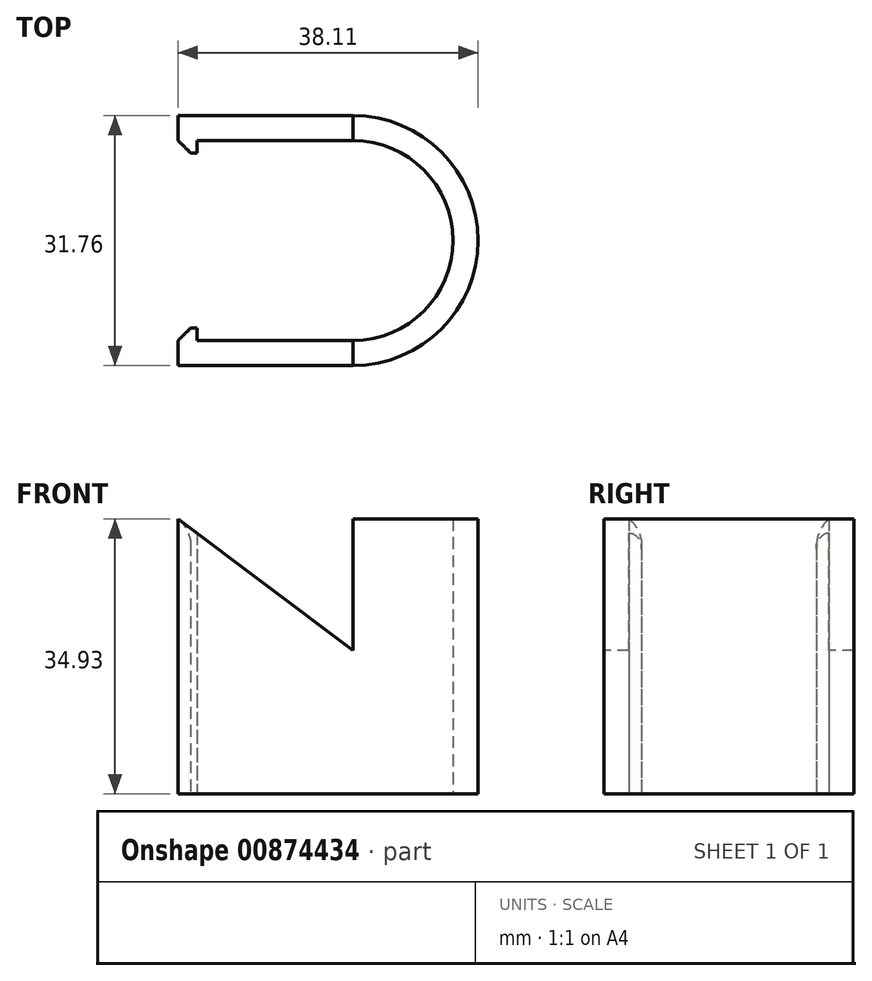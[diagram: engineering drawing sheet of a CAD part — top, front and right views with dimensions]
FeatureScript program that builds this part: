
annotation { "Feature Type Name" : "Feature", "Feature Type Description" : "" }
export const myFeature = defineFeature(function(context is Context, id is Id, definition is map)
    precondition{}
    {
        {
            var Q0;
            Q0=qCreatedBy(makeId("Top.planeOp"),FACE);
            var sketch = newSketch(context, id + "F0", { "sketchPlane" : qUnion([Q0])});
            skLineSegment(sketch, "E0.bottom", {"start": v(-22.22, 15.88) * mm, "end": v(0, 15.87) * mm});
            skLineSegment(sketch, "E0.left", {"start": v(-22.22, 15.87) * mm, "end": v(-22.22, 12.7) * mm});
            skLineSegment(sketch, "E0.right", {"start": v(15.88, 0) * mm, "end": v(15.88, 0) * mm});
            skPoint(sketch, "E1.visualSharp", {"position": v(15.88, 15.88) * mm});
            skArc(sketch, "E1.filletArc", {"start": v(15.88, 0) * mm, "mid": v(11.23, 11.23) * mm, "end": v(0, 15.88) * mm});
            skArc(sketch, "E2.0", {"start": v(12.7, 0) * mm, "mid": v(8.98, 8.98) * mm, "end": v(0, 12.7) * mm});
            skLineSegment(sketch, "E2.1", {"start": v(-19.84, 12.7) * mm, "end": v(0, 12.7) * mm});
            skLineSegment(sketch, "E3", {"start": v(0, 0) * mm, "end": v(15.88, 0) * mm, "construction": true});
            skLineSegment(sketch, "E4", {"start": v(-22.22, 12.7) * mm, "end": v(-20.64, 11.11) * mm});
            skLineSegment(sketch, "E5", {"start": v(-19.84, 12.7) * mm, "end": v(-19.84, 11.11) * mm});
            skLineSegment(sketch, "E6", {"start": v(-20.64, 11.11) * mm, "end": v(-19.84, 11.11) * mm});
            skLineSegment(sketch, "E7.MirrorCS", {"start": v(-22.23, -15.87) * mm, "end": v(-22.23, -12.7) * mm});
            skLineSegment(sketch, "E8.MirrorCS", {"start": v(-22.22, -12.7) * mm, "end": v(-20.64, -11.11) * mm});
            skLineSegment(sketch, "E9.MirrorCS", {"start": v(-20.64, -11.11) * mm, "end": v(-19.84, -11.11) * mm});
            skLineSegment(sketch, "E10.MirrorCS", {"start": v(-19.84, -12.7) * mm, "end": v(-19.84, -11.11) * mm});
            skLineSegment(sketch, "E11.MirrorCS", {"start": v(-22.22, -15.87) * mm, "end": v(0, -15.87) * mm});
            skPoint(sketch, "E12.MirrorP", {"position": v(15.88, -15.88) * mm});
            skLineSegment(sketch, "E13.MirrorCS", {"start": v(-19.84, -12.7) * mm, "end": v(0, -12.7) * mm});
            skArc(sketch, "E14.MirrorCS", {"start": v(12.7, 0) * mm, "mid": v(8.98, -8.98) * mm, "end": v(0, -12.7) * mm});
            skArc(sketch, "E15.MirrorCS", {"start": v(15.88, 0) * mm, "mid": v(11.23, -11.23) * mm, "end": v(0, -15.88) * mm});
            skSolve(sketch);
        }
        {
            var Q0;
            Q0=makeQuery(id+"F0.imprint","IMPRINT",FACE,{"disambiguationData":[TD([[makeQuery(id+"F0.imprint","IMPRINT",EDGE,{"derivedFrom":sQuery(id+"F0.wireOp",EDGE,"E0.bottom")}),-1.0]])]});
            extrude(context, id + "F1", {"entities" : qUnion([Q0]), "depth" : 34.92 * mm, "offsetDistance" : 25.4 * mm});
        }
        {
            var Q0;
            Q0=makeQuery(id+"F1.opExtrude","SWEPT_FACE",FACE,{"disambiguationData":[OSD([sQuery(id+"F0.wireOp",EDGE,"E11.MirrorCS")])]});
            var sketch = newSketch(context, id + "F2", { "sketchPlane" : qUnion([Q0])});
            skLineSegment(sketch, "E16", {"start": v(15.88, 34.93) * mm, "end": v(15.88, 0) * mm});
            skLineSegment(sketch, "E17.0", {"start": v(0, 34.93) * mm, "end": v(15.88, 34.93) * mm});
            skLineSegment(sketch, "E18.0", {"start": v(-22.22, 34.93) * mm, "end": v(0, 34.93) * mm});
            skLineSegment(sketch, "E19.0", {"start": v(-22.22, 34.93) * mm, "end": v(-22.22, 0) * mm});
            skLineSegment(sketch, "E20.0", {"start": v(-22.22, 0) * mm, "end": v(0, 0) * mm});
            skLineSegment(sketch, "E21.0", {"start": v(0, 0) * mm, "end": v(15.88, 0) * mm});
            skLineSegment(sketch, "E22", {"start": v(-22.22, 19.05) * mm, "end": v(-22.22, 0) * mm});
            skLineSegment(sketch, "E23", {"start": v(-22.22, 0) * mm, "end": v(15.88, 0) * mm});
            skLineSegment(sketch, "E24", {"start": v(15.88, 0) * mm, "end": v(-22.23, 19.05) * mm});
            skLineSegment(sketch, "E25", {"start": v(-22.23, 34.93) * mm, "end": v(15.88, 6.35) * mm});
            skLineSegment(sketch, "E26", {"start": v(15.88, 6.35) * mm, "end": v(15.88, 34.93) * mm});
            skLineSegment(sketch, "E27", {"start": v(15.88, 34.93) * mm, "end": v(-22.22, 34.93) * mm});
            skSolve(sketch);
        }
        {
            var Q0;
            {var subQ0=sQuery(id+"F2.wireOp",EDGE,"E27");var subQ1=sQuery(id+"F2.wireOp",EDGE,"E25");var subQ2=makeQuery(id+"F2.imprint","INTERSECT",VERTEX,{"derivedFrom":[sQuery(id+"F2.wireOp",EDGE,"E19.0"),subQ1,subQ0]});Q0=makeQuery(id+"F2.imprint","IMPRINT",FACE,{"disambiguationData":[TD([[makeQuery(id+"F2.imprint","IMPRINT",EDGE,{"disambiguationData":[TD([[subQ2,-1.0]])],"derivedFrom":subQ1}),1.0]])]});}
            var Q1;
            {var subQ0=sQuery(id+"F2.wireOp",EDGE,"E26");Q1=makeQuery(id+"F2.imprint","IMPRINT",FACE,{"disambiguationData":[TD([[makeQuery(id+"F2.imprint","IMPRINT",EDGE,{"derivedFrom":subQ0}),1.0]])]});}
            var Q2;
            {var subQ0=sQuery(id+"F2.wireOp",EDGE,"E22");Q2=makeQuery(id+"F2.imprint","IMPRINT",FACE,{"disambiguationData":[TD([[makeQuery(id+"F2.imprint","IMPRINT",EDGE,{"derivedFrom":subQ0}),1.0]])]});}
            var Q3;
            {var subQ0=sQuery(id+"F2.wireOp",EDGE,"E23");var subQ1=makeQuery(id+"F1.opExtrude","SWEPT_EDGE",EDGE,{"disambiguationData":[OSD([sQuery(id+"F0.wireOp",EDGE,"E11.MirrorCS"),sQuery(id+"F0.wireOp",EDGE,"E15.MirrorCS")])]});var subQ2=makeQuery(id+"F2.imprint","INTERSECT",VERTEX,{"derivedFrom":[subQ1,subQ0]});Q3=makeQuery(id+"F2.imprint","IMPRINT",FACE,{"disambiguationData":[TD([[makeQuery(id+"F2.imprint","IMPRINT",EDGE,{"disambiguationData":[TD([[subQ2,-1.0]])],"derivedFrom":subQ0}),1.0]])]});}
            var Q4;
            Q4=makeQuery(id+"F1.opExtrude","SWEPT_FACE",FACE,{"disambiguationData":[OSD([sQuery(id+"F0.wireOp",EDGE,"E0.bottom")])]});
            extrude(context, id + "F3", {"entities" : qUnion([Q0, Q1, Q2, Q3]), "operationType" : NewBodyOperationType.REMOVE, "endBound" : BoundingType.UP_TO_SURFACE, "oppositeDirection" : true, "depth" : 31.75 * mm, "endBoundEntityFace" : qUnion([Q4]), "offsetDistance" : 25.4 * mm});
        }
        {
            var Q0;
            Q0=makeQuery(id+"F3.boolean.opBoolean","INTERSECT",EDGE,{"derivedFrom":[makeQuery(id+"F1.opExtrude","SWEPT_FACE",FACE,{"disambiguationData":[OSD([sQuery(id+"F0.wireOp",EDGE,"E6")])]}),makeQuery(id+"F3.opExtrude","SWEPT_FACE",FACE,{"disambiguationData":[OSD([sQuery(id+"F2.wireOp",EDGE,"E25")])]})]});
            var Q1;
            Q1=makeQuery(id+"F3.boolean.opBoolean","INTERSECT",EDGE,{"derivedFrom":[makeQuery(id+"F1.opExtrude","SWEPT_FACE",FACE,{"disambiguationData":[OSD([sQuery(id+"F0.wireOp",EDGE,"E9.MirrorCS")])]}),makeQuery(id+"F3.opExtrude","SWEPT_FACE",FACE,{"disambiguationData":[OSD([sQuery(id+"F2.wireOp",EDGE,"E25")])]})]});
            fillet(context, id + "F4", {"entities" : qUnion([Q0, Q1]), "radius" : 1.59 * mm, "tangentPropagation" : true, "allowEdgeOverflow" : false});
        }
    });
